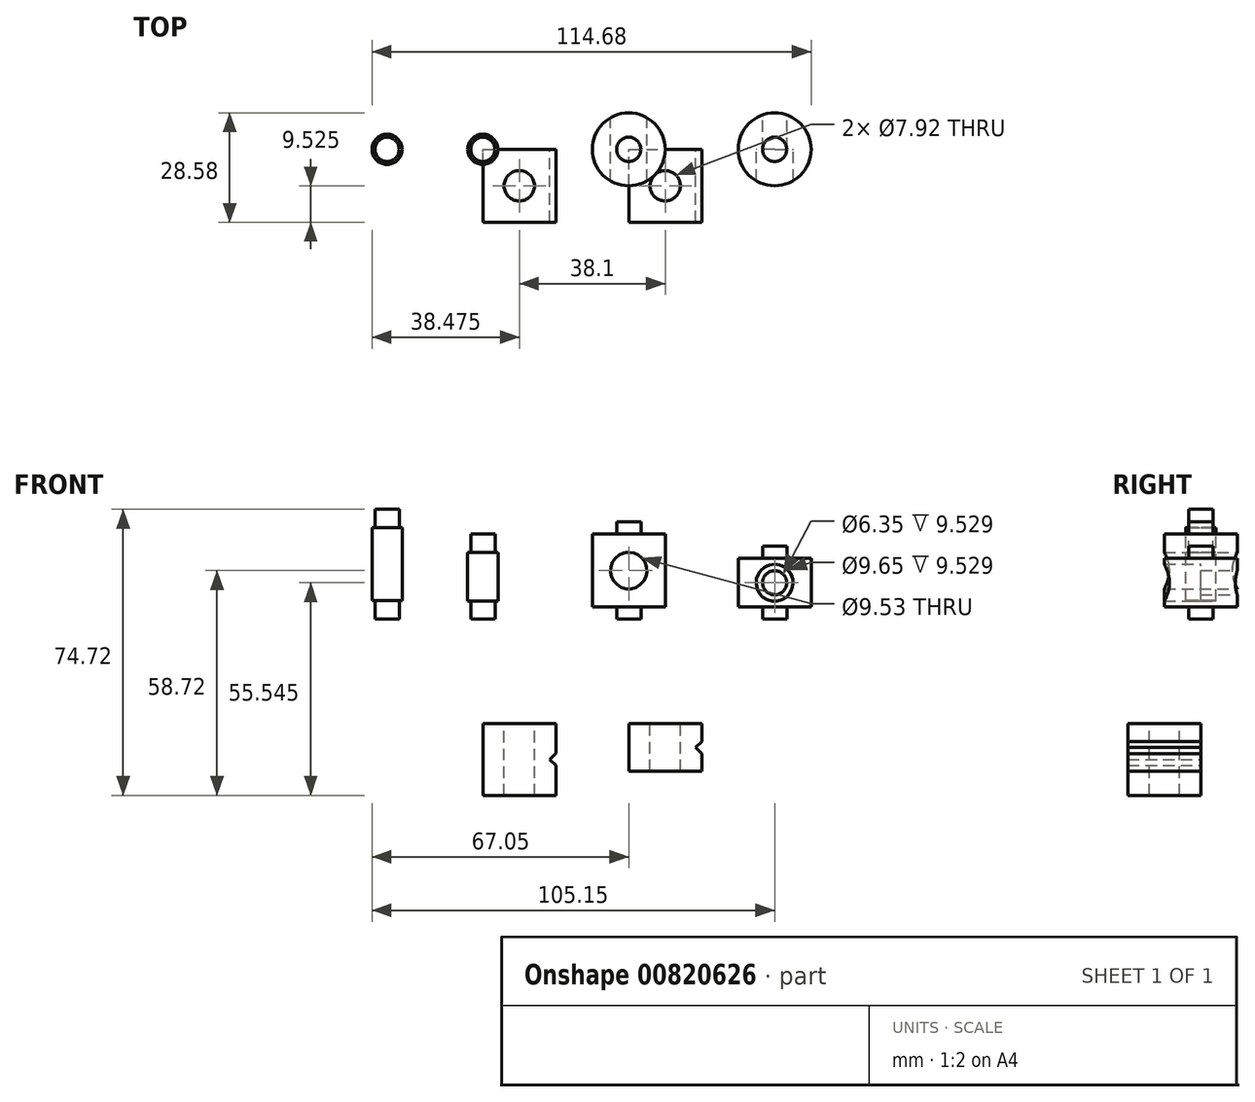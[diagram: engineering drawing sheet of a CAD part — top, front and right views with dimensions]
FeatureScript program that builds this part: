
annotation { "Feature Type Name" : "Feature", "Feature Type Description" : "" }
export const myFeature = defineFeature(function(context is Context, id is Id, definition is map)
    precondition{}
    {
        {
            var Q0;
            Q0=qCreatedBy(makeId("Front.planeOp"),FACE);
            var sketch = newSketch(context, id + "F0", { "sketchPlane" : qUnion([Q0])});
            skLineSegment(sketch, "E0", {"start": v(0, 0) * mm, "end": v(-3.18, 0) * mm});
            skLineSegment(sketch, "E1", {"start": v(-3.18, 0) * mm, "end": v(-3.18, 3.18) * mm});
            skLineSegment(sketch, "E2", {"start": v(-3.18, 3.18) * mm, "end": v(-9.53, 3.18) * mm});
            skLineSegment(sketch, "E3", {"start": v(-9.53, 3.18) * mm, "end": v(-9.53, 22.23) * mm});
            skLineSegment(sketch, "E4", {"start": v(-9.53, 22.23) * mm, "end": v(-3.18, 22.23) * mm});
            skLineSegment(sketch, "E5", {"start": v(-3.18, 22.23) * mm, "end": v(-3.18, 25.4) * mm});
            skLineSegment(sketch, "E6", {"start": v(-3.18, 25.4) * mm, "end": v(0, 25.4) * mm});
            skLineSegment(sketch, "E7", {"start": v(0, 25.4) * mm, "end": v(0, 0) * mm});
            skCircle(sketch, "E8", {"center": v(0, 12.7) * mm, "radius": 4.76 * mm});
            skLineSegment(sketch, "E9", {"start": v(34.92, 0) * mm, "end": v(34.92, 3.17) * mm});
            skLineSegment(sketch, "E10", {"start": v(34.92, 3.17) * mm, "end": v(28.58, 3.17) * mm});
            skLineSegment(sketch, "E11", {"start": v(28.58, 3.17) * mm, "end": v(28.58, 15.88) * mm});
            skLineSegment(sketch, "E12", {"start": v(28.58, 15.88) * mm, "end": v(34.92, 15.88) * mm});
            skLineSegment(sketch, "E13", {"start": v(34.92, 15.88) * mm, "end": v(34.92, 19.05) * mm});
            skLineSegment(sketch, "E14", {"start": v(34.92, 19.05) * mm, "end": v(38.1, 19.05) * mm});
            skLineSegment(sketch, "E15", {"start": v(38.1, 19.05) * mm, "end": v(38.1, 0) * mm});
            skLineSegment(sketch, "E16", {"start": v(38.1, 0) * mm, "end": v(34.92, 0) * mm});
            skCircle(sketch, "E17", {"center": v(38.1, 9.53) * mm, "radius": 4.83 * mm});
            skCircle(sketch, "E18", {"center": v(38.1, 9.53) * mm, "radius": 3.18 * mm});
            skLineSegment(sketch, "E19", {"start": v(-41.27, 0) * mm, "end": v(-41.27, 4.76) * mm});
            skLineSegment(sketch, "E20", {"start": v(-41.27, 4.76) * mm, "end": v(-42.04, 4.76) * mm});
            skLineSegment(sketch, "E21", {"start": v(-42.04, 4.76) * mm, "end": v(-42.04, 17.46) * mm});
            skLineSegment(sketch, "E22", {"start": v(-42.04, 17.46) * mm, "end": v(-41.27, 17.46) * mm});
            skLineSegment(sketch, "E23", {"start": v(-41.27, 17.46) * mm, "end": v(-41.27, 22.23) * mm});
            skLineSegment(sketch, "E24", {"start": v(-41.27, 22.23) * mm, "end": v(-38.1, 22.23) * mm});
            skLineSegment(sketch, "E25", {"start": v(-38.1, 22.23) * mm, "end": v(-38.1, 0) * mm});
            skLineSegment(sketch, "E26", {"start": v(-38.1, 0) * mm, "end": v(-41.27, 0) * mm});
            skLineSegment(sketch, "E27", {"start": v(-66.29, 0) * mm, "end": v(-66.29, 4.83) * mm});
            skLineSegment(sketch, "E28", {"start": v(-66.29, 4.83) * mm, "end": v(-67.05, 4.83) * mm});
            skLineSegment(sketch, "E29", {"start": v(-67.05, 4.83) * mm, "end": v(-67.05, 23.88) * mm});
            skLineSegment(sketch, "E30", {"start": v(-67.05, 23.88) * mm, "end": v(-66.29, 23.88) * mm});
            skLineSegment(sketch, "E31", {"start": v(-66.29, 23.88) * mm, "end": v(-66.29, 28.7) * mm});
            skLineSegment(sketch, "E32", {"start": v(-66.29, 28.7) * mm, "end": v(-63.11, 28.7) * mm});
            skLineSegment(sketch, "E33", {"start": v(-63.11, 28.7) * mm, "end": v(-63.11, 0) * mm});
            skLineSegment(sketch, "E34", {"start": v(-63.11, 0) * mm, "end": v(-66.29, 0) * mm});
            skLineSegment(sketch, "E35.bottom", {"start": v(0, -27.22) * mm, "end": v(19.05, -27.22) * mm});
            skLineSegment(sketch, "E35.top", {"start": v(0, -39.67) * mm, "end": v(19.05, -39.67) * mm});
            skLineSegment(sketch, "E35.left", {"start": v(0, -27.22) * mm, "end": v(0, -39.67) * mm});
            skLineSegment(sketch, "E35.right", {"start": v(19.05, -27.22) * mm, "end": v(19.05, -31.92) * mm});
            skLineSegment(sketch, "E36.bottom", {"start": v(-38.1, -27.22) * mm, "end": v(-19.05, -27.22) * mm});
            skLineSegment(sketch, "E36.top", {"start": v(-38.1, -46.02) * mm, "end": v(-19.05, -46.02) * mm});
            skLineSegment(sketch, "E36.left", {"start": v(-38.1, -27.22) * mm, "end": v(-38.1, -46.02) * mm});
            skLineSegment(sketch, "E36.right", {"start": v(-19.05, -27.22) * mm, "end": v(-19.05, -34.97) * mm});
            skLineSegment(sketch, "E37", {"start": v(-19.05, -36.62) * mm, "end": v(-38.1, -36.62) * mm, "construction": true});
            skLineSegment(sketch, "E38", {"start": v(0, -33.45) * mm, "end": v(19.05, -33.45) * mm, "construction": true});
            skLineSegment(sketch, "E39", {"start": v(-19.05, -38.14) * mm, "end": v(-20.64, -36.62) * mm});
            skLineSegment(sketch, "E40", {"start": v(-20.64, -36.62) * mm, "end": v(-19.05, -34.97) * mm});
            skLineSegment(sketch, "E41", {"start": v(19.05, -31.92) * mm, "end": v(17.46, -33.45) * mm});
            skLineSegment(sketch, "E42", {"start": v(17.46, -33.45) * mm, "end": v(19.05, -35.1) * mm});
            skLineSegment(sketch, "E43.trimOffspring", {"start": v(-19.05, -38.14) * mm, "end": v(-19.05, -46.02) * mm});
            skLineSegment(sketch, "E44.trimOffspring", {"start": v(19.05, -35.1) * mm, "end": v(19.05, -39.67) * mm});
            skSolve(sketch);
        }
        {
            var Q0;
            {var subQ0=sQuery(id+"F0.wireOp",EDGE,"E0");Q0=makeQuery(id+"F0.imprint","IMPRINT",FACE,{"disambiguationData":[TD([[makeQuery(id+"F0.imprint","IMPRINT",EDGE,{"derivedFrom":subQ0}),-1.0]])]});}
            var Q1;
            {var subQ0=sQuery(id+"F0.wireOp",EDGE,"E8");var subQ1=sQuery(id+"F0.wireOp",EDGE,"E7");var subQ2=makeQuery(id+"F0.imprint","INTERSECT",VERTEX,{"disambiguationData":[OD(0.0)],"derivedFrom":[subQ1,subQ0]});Q1=makeQuery(id+"F0.imprint","IMPRINT",FACE,{"disambiguationData":[TD([[makeQuery(id+"F0.imprint","IMPRINT",EDGE,{"disambiguationData":[TD([[subQ2,-1.0]])],"derivedFrom":subQ1}),-1.0]])]});}
            var Q2;
            Q2=sQuery(id+"F0.wireOp",EDGE,"E7");
            revolve(context, id + "F1", {"surfaceOperationType" : NewSurfaceOperationType.NEW, "entities" : qUnion([Q0, Q1]), "axis" : qUnion([Q2]), "revolveType" : RevolveType.FULL});
        }
        {
            var Q0;
            {var subQ0=sQuery(id+"F0.wireOp",EDGE,"E8");var subQ1=sQuery(id+"F0.wireOp",EDGE,"E7");var subQ2=makeQuery(id+"F0.imprint","INTERSECT",VERTEX,{"disambiguationData":[OD(0.0)],"derivedFrom":[subQ1,subQ0]});Q0=makeQuery(id+"F0.imprint","IMPRINT",FACE,{"disambiguationData":[TD([[makeQuery(id+"F0.imprint","IMPRINT",EDGE,{"disambiguationData":[TD([[subQ2,-1.0]])],"derivedFrom":subQ1}),-1.0]])]});}
            var Q1;
            {var subQ0=sQuery(id+"F0.wireOp",EDGE,"E8");var subQ1=sQuery(id+"F0.wireOp",EDGE,"E7");var subQ2=makeQuery(id+"F0.imprint","INTERSECT",VERTEX,{"disambiguationData":[OD(0.0)],"derivedFrom":[subQ1,subQ0]});Q1=makeQuery(id+"F0.imprint","IMPRINT",FACE,{"disambiguationData":[TD([[makeQuery(id+"F0.imprint","IMPRINT",EDGE,{"disambiguationData":[TD([[subQ2,-1.0]])],"derivedFrom":subQ1}),1.0]])]});}
            var Q2;
            Q2=sQuery(id+"F0.wireOp",EDGE,"E8");
            extrude(context, id + "F2", {"entities" : qUnion([Q0, Q1]), "operationType" : NewBodyOperationType.REMOVE, "surfaceOperationType" : NewSurfaceOperationType.ADD, "surfaceEntities" : qUnion([Q2]), "depth" : 25.4 * mm, "offsetDistance" : 25.4 * mm, "symmetric" : true});
        }
        {
            var Q0;
            Q0=makeQuery(id+"F0.imprint","IMPRINT",FACE,{"disambiguationData":[TD([[makeQuery(id+"F0.imprint","IMPRINT",EDGE,{"derivedFrom":sQuery(id+"F0.wireOp",EDGE,"E9")}),-1.0]])]});
            var Q1;
            {var subQ0=sQuery(id+"F0.wireOp",EDGE,"E17");var subQ1=sQuery(id+"F0.wireOp",EDGE,"E15");var subQ2=makeQuery(id+"F0.imprint","INTERSECT",VERTEX,{"disambiguationData":[OD(0.0)],"derivedFrom":[subQ1,subQ0]});Q1=makeQuery(id+"F0.imprint","IMPRINT",FACE,{"disambiguationData":[TD([[makeQuery(id+"F0.imprint","IMPRINT",EDGE,{"disambiguationData":[TD([[subQ2,-1.0]])],"derivedFrom":subQ1}),-1.0]])]});}
            var Q2;
            Q2=sQuery(id+"F0.wireOp",EDGE,"E15");
            revolve(context, id + "F3", {"surfaceOperationType" : NewSurfaceOperationType.NEW, "entities" : qUnion([Q0, Q1]), "axis" : qUnion([Q2]), "revolveType" : RevolveType.FULL});
        }
        {
            var Q0;
            {var subQ0=sQuery(id+"F0.wireOp",EDGE,"E18");var subQ1=sQuery(id+"F0.wireOp",EDGE,"E15");var subQ2=makeQuery(id+"F0.imprint","INTERSECT",VERTEX,{"disambiguationData":[OD(0.0)],"derivedFrom":[subQ1,subQ0]});Q0=makeQuery(id+"F0.imprint","IMPRINT",FACE,{"disambiguationData":[TD([[makeQuery(id+"F0.imprint","IMPRINT",EDGE,{"disambiguationData":[TD([[subQ2,-1.0]])],"derivedFrom":subQ1}),1.0]])]});}
            var Q1;
            {var subQ0=sQuery(id+"F0.wireOp",EDGE,"E18");var subQ1=sQuery(id+"F0.wireOp",EDGE,"E15");var subQ2=makeQuery(id+"F0.imprint","INTERSECT",VERTEX,{"disambiguationData":[OD(0.0)],"derivedFrom":[subQ1,subQ0]});Q1=makeQuery(id+"F0.imprint","IMPRINT",FACE,{"disambiguationData":[TD([[makeQuery(id+"F0.imprint","IMPRINT",EDGE,{"disambiguationData":[TD([[subQ2,-1.0]])],"derivedFrom":subQ1}),-1.0]])]});}
            extrude(context, id + "F4", {"entities" : qUnion([Q0, Q1]), "operationType" : NewBodyOperationType.REMOVE, "endBound" : BoundingType.THROUGH_ALL, "depth" : 25.4 * mm, "offsetDistance" : 25.4 * mm, "hasSecondDirection" : true, "secondDirectionBound" : BoundingType.THROUGH_ALL, "secondDirectionOppositeDirection" : true, "secondDirectionDepth" : 25.4 * mm});
        }
        {
            var Q0;
            {var subQ0=sQuery(id+"F0.wireOp",EDGE,"E17");var subQ1=sQuery(id+"F0.wireOp",EDGE,"E15");var subQ2=makeQuery(id+"F0.imprint","INTERSECT",VERTEX,{"disambiguationData":[OD(0.0)],"derivedFrom":[subQ1,subQ0]});Q0=makeQuery(id+"F0.imprint","IMPRINT",FACE,{"disambiguationData":[TD([[makeQuery(id+"F0.imprint","IMPRINT",EDGE,{"disambiguationData":[TD([[subQ2,-1.0]])],"derivedFrom":subQ1}),-1.0]])]});}
            var Q1;
            {var subQ0=sQuery(id+"F0.wireOp",EDGE,"E17");var subQ1=sQuery(id+"F0.wireOp",EDGE,"E15");var subQ2=makeQuery(id+"F0.imprint","INTERSECT",VERTEX,{"disambiguationData":[OD(0.0)],"derivedFrom":[subQ1,subQ0]});Q1=makeQuery(id+"F0.imprint","IMPRINT",FACE,{"disambiguationData":[TD([[makeQuery(id+"F0.imprint","IMPRINT",EDGE,{"disambiguationData":[TD([[subQ2,-1.0]])],"derivedFrom":subQ1}),1.0]])]});}
            extrude(context, id + "F5", {"entities" : qUnion([Q0, Q1]), "operationType" : NewBodyOperationType.REMOVE, "endBound" : BoundingType.THROUGH_ALL, "depth" : 25.4 * mm, "offsetDistance" : 25.4 * mm});
        }
        {
            var Q0;
            Q0=makeQuery(id+"F0.imprint","IMPRINT",FACE,{"disambiguationData":[TD([[makeQuery(id+"F0.imprint","IMPRINT",EDGE,{"derivedFrom":sQuery(id+"F0.wireOp",EDGE,"E19")}),-1.0]])]});
            var Q1;
            Q1=sQuery(id+"F0.wireOp",EDGE,"E25");
            revolve(context, id + "F6", {"surfaceOperationType" : NewSurfaceOperationType.NEW, "entities" : qUnion([Q0]), "axis" : qUnion([Q1]), "revolveType" : RevolveType.FULL});
        }
        {
            var Q0;
            Q0=makeQuery(id+"F0.imprint","IMPRINT",FACE,{"disambiguationData":[TD([[makeQuery(id+"F0.imprint","IMPRINT",EDGE,{"derivedFrom":sQuery(id+"F0.wireOp",EDGE,"E27")}),-1.0]])]});
            var Q1;
            Q1=sQuery(id+"F0.wireOp",EDGE,"E33");
            revolve(context, id + "F7", {"surfaceOperationType" : NewSurfaceOperationType.NEW, "entities" : qUnion([Q0]), "axis" : qUnion([Q1]), "revolveType" : RevolveType.FULL});
        }
        {
            var Q0;
            Q0=makeQuery(id+"F0.imprint","IMPRINT",FACE,{"disambiguationData":[TD([[makeQuery(id+"F0.imprint","IMPRINT",EDGE,{"derivedFrom":sQuery(id+"F0.wireOp",EDGE,"E36.bottom")}),-1.0]])]});
            extrude(context, id + "F8", {"entities" : qUnion([Q0]), "depth" : 19.05 * mm, "offsetDistance" : 25.4 * mm});
        }
        {
            var Q0;
            Q0=makeQuery(id+"F0.imprint","IMPRINT",FACE,{"disambiguationData":[TD([[makeQuery(id+"F0.imprint","IMPRINT",EDGE,{"derivedFrom":sQuery(id+"F0.wireOp",EDGE,"E35.bottom")}),-1.0]])]});
            extrude(context, id + "F9", {"entities" : qUnion([Q0]), "depth" : 19.05 * mm, "offsetDistance" : 25.4 * mm});
        }
        {
            var Q0;
            Q0=makeQuery(id+"F8.opExtrude","SWEPT_FACE",FACE,{"disambiguationData":[OSD([sQuery(id+"F0.wireOp",EDGE,"E36.bottom")])]});
            var sketch = newSketch(context, id + "F10", { "sketchPlane" : qUnion([Q0])});
            skLineSegment(sketch, "E45", {"start": v(-28.57, 0) * mm, "end": v(-28.57, -19.05) * mm, "construction": true});
            skCircle(sketch, "E46", {"center": v(-28.57, -9.53) * mm, "radius": 3.96 * mm});
            skSolve(sketch);
        }
        {
            var Q0;
            Q0=makeQuery(id+"F10.imprint","IMPRINT",FACE,{"disambiguationData":[TD([[makeQuery(id+"F10.imprint","IMPRINT",EDGE,{"derivedFrom":sQuery(id+"F10.wireOp",EDGE,"E46")}),1.0]])]});
            extrude(context, id + "F11", {"entities" : qUnion([Q0]), "operationType" : NewBodyOperationType.REMOVE, "endBound" : BoundingType.THROUGH_ALL, "oppositeDirection" : true, "depth" : 25.4 * mm, "offsetDistance" : 25.4 * mm});
        }
        {
            var Q0;
            Q0=makeQuery(id+"F9.opExtrude","SWEPT_FACE",FACE,{"disambiguationData":[OSD([sQuery(id+"F0.wireOp",EDGE,"E35.bottom")])]});
            var sketch = newSketch(context, id + "F12", { "sketchPlane" : qUnion([Q0])});
            skLineSegment(sketch, "E47", {"start": v(9.53, 0) * mm, "end": v(9.53, -19.05) * mm, "construction": true});
            skCircle(sketch, "E48", {"center": v(9.53, -9.53) * mm, "radius": 3.96 * mm});
            skSolve(sketch);
        }
        {
            var Q0;
            Q0=makeQuery(id+"F12.imprint","IMPRINT",FACE,{"disambiguationData":[TD([[makeQuery(id+"F12.imprint","IMPRINT",EDGE,{"derivedFrom":sQuery(id+"F12.wireOp",EDGE,"E48")}),1.0]])]});
            extrude(context, id + "F13", {"entities" : qUnion([Q0]), "operationType" : NewBodyOperationType.REMOVE, "endBound" : BoundingType.THROUGH_ALL, "oppositeDirection" : true, "depth" : 25.4 * mm, "offsetDistance" : 25.4 * mm});
        }
    });
